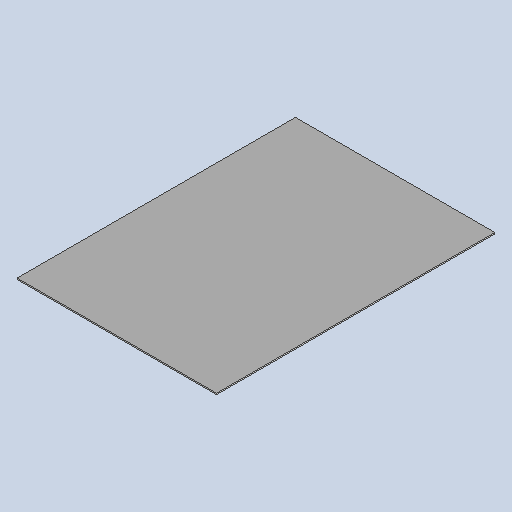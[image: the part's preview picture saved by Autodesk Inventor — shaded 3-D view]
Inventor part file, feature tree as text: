
AUTODESK INVENTOR PART (.ipt)
format: ipt  version: 2025 (Build 290162010, 162A)  size: 246,272 bytes
history: native  units: mm
features: other x4, sketch x2, sheet_metal_op x1
ambient origin geometry x8: Origin, YZ Plane, XZ Plane, XY Plane, X Axis, Y Axis, Z Axis, Center Point
bodies: Solid1 (feature_tree)
feature tree (7):
  sheet_metal_op  "Face1"
  other  "Mark1"
  other  "A-Side Definition"
  sketch  "Sketch1"  dims[d0=480.0mm]
  other  "Plate1"
  sketch  "Sketch2"  dims[d1=670.0mm d2=3.0mm d6=200.0mm d9=20.0mm d10=20.0mm d11=20.0mm]
  other  "Definition1"
